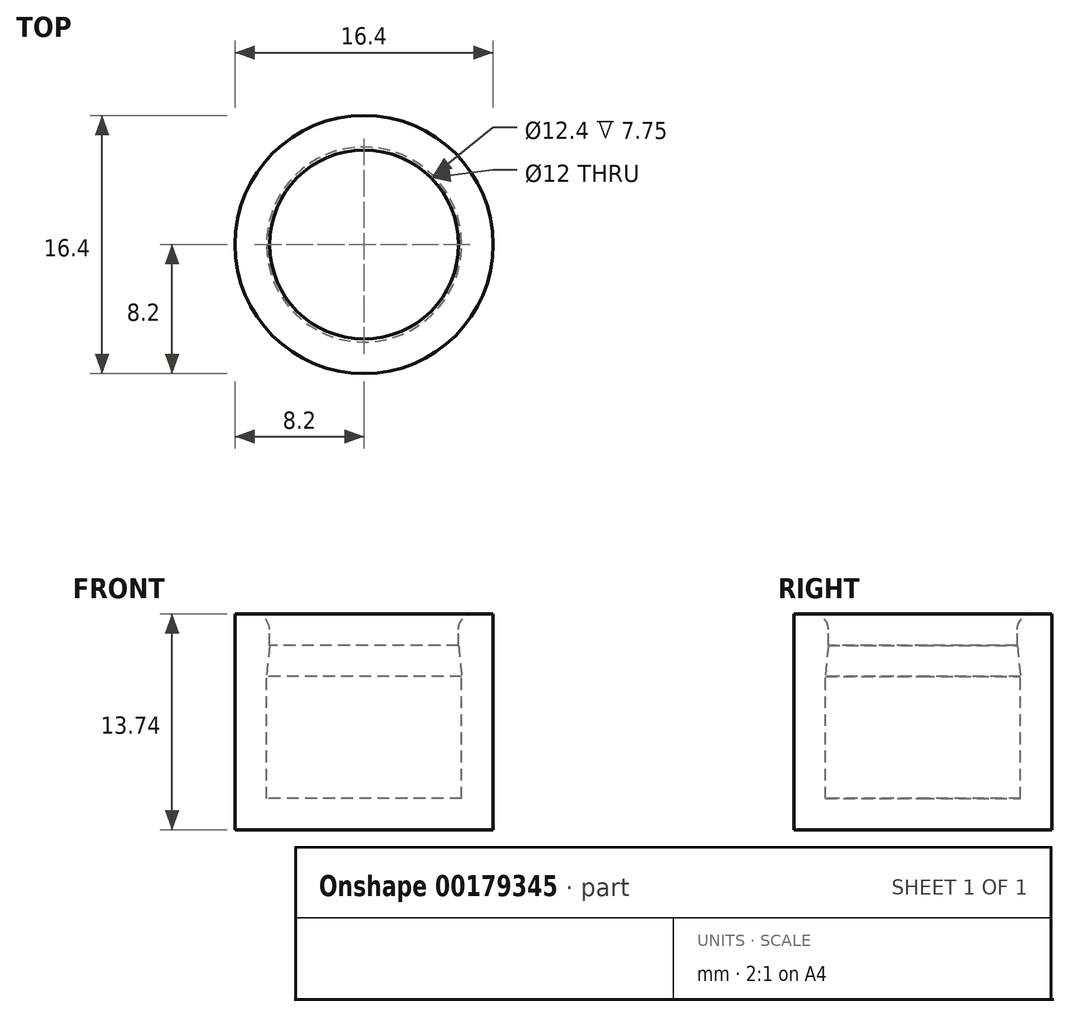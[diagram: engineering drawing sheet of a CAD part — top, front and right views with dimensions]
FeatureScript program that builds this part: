
annotation { "Feature Type Name" : "Feature", "Feature Type Description" : "" }
export const myFeature = defineFeature(function(context is Context, id is Id, definition is map)
    precondition{}
    {
        {
            var Q0;
            Q0=qCreatedBy(makeId("Front.planeOp"),FACE);
            var sketch = newSketch(context, id + "F0", { "sketchPlane" : qUnion([Q0])});
            skLineSegment(sketch, "E0", {"start": v(0, 0) * mm, "end": v(-8.2, 0) * mm});
            skLineSegment(sketch, "E1", {"start": v(-8.2, 0) * mm, "end": v(-8.2, 13.74) * mm});
            skLineSegment(sketch, "E2", {"start": v(-8.2, 13.74) * mm, "end": v(-6, 13.74) * mm});
            skLineSegment(sketch, "E3", {"start": v(-6, 13.74) * mm, "end": v(-6, 11.74) * mm});
            skLineSegment(sketch, "E4", {"start": v(-6, 11.74) * mm, "end": v(-6.2, 9.75) * mm});
            skLineSegment(sketch, "E5", {"start": v(-6.2, 9.75) * mm, "end": v(-6.2, 2) * mm});
            skLineSegment(sketch, "E6", {"start": v(-6.2, 2) * mm, "end": v(0, 2) * mm});
            skLineSegment(sketch, "E7", {"start": v(0, 2) * mm, "end": v(0, 0) * mm});
            skLineSegment(sketch, "E8", {"start": v(-6.2, 2) * mm, "end": v(-8.2, 2) * mm, "construction": true});
            skLineSegment(sketch, "E9", {"start": v(-6, 13.74) * mm, "end": v(0, 13.74) * mm, "construction": true});
            skLineSegment(sketch, "E10", {"start": v(-6.2, 9.75) * mm, "end": v(0, 9.75) * mm, "construction": true});
            skSolve(sketch);
        }
        {
            var Q0;
            Q0 = qSketchRegion(id + "F0", true);
            var Q1;
            Q1=sQuery(id+"F0.wireOp",EDGE,"E7");
            revolve(context, id + "F1", {"entities" : qUnion([Q0]), "axis" : qUnion([Q1]), "revolveType" : RevolveType.FULL});
        }
        {
            var Q0;
            Q0=makeQuery(id+"F1.opRevolve","SWEPT_EDGE",EDGE,{"disambiguationData":[OSD([sQuery(id+"F0.wireOp",EDGE,"E2"),sQuery(id+"F0.wireOp",EDGE,"E3")])]});
            fillet(context, id + "F2", {"entities" : qUnion([Q0]), "radius" : 1 * mm, "tangentPropagation" : true, "allowEdgeOverflow" : false});
        }
    });
